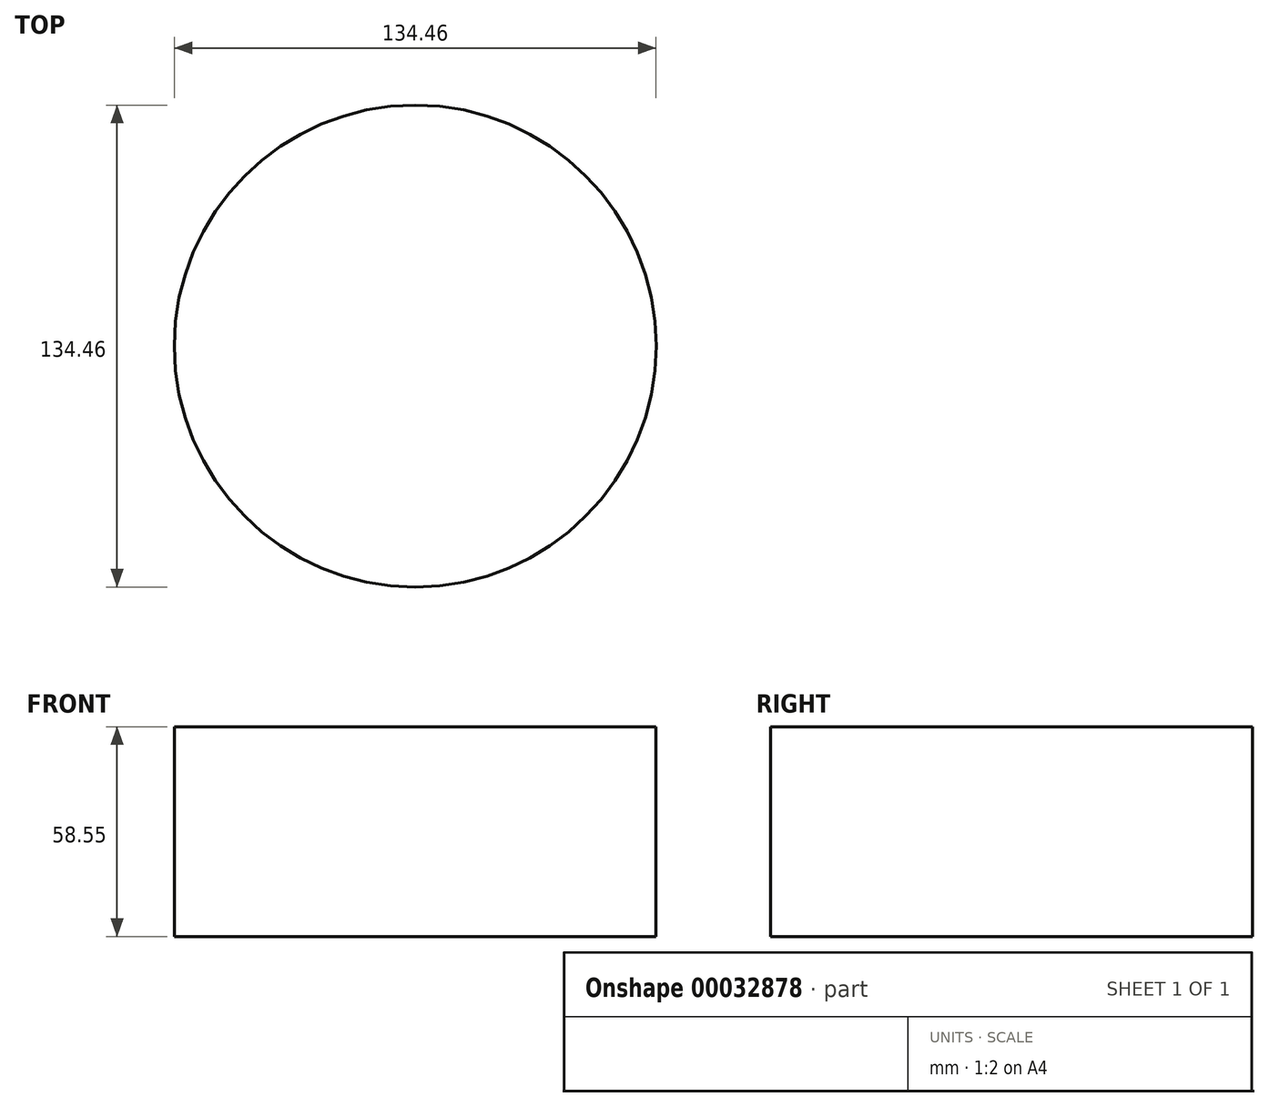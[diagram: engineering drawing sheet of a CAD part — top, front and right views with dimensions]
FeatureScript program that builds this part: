
annotation { "Feature Type Name" : "Feature", "Feature Type Description" : "" }
export const myFeature = defineFeature(function(context is Context, id is Id, definition is map)
    precondition{}
    {
        {
            var Q0;
            Q0=qCreatedBy(makeId("Top.planeOp"),FACE);
            var sketch = newSketch(context, id + "F0", { "sketchPlane" : qUnion([Q0])});
            skCircle(sketch, "E0", {"center": v(2.86, 0) * mm, "radius": 67.23 * mm});
            skSolve(sketch);
        }
        {
            var Q0;
            Q0=sQuery(id+"F0.wireOp",EDGE,"E0");
            extrude(context, id + "F1", {"bodyType" : ToolBodyType.SURFACE, "surfaceEntities" : qUnion([Q0]), "depth" : 58.55 * mm});
        }
    });
